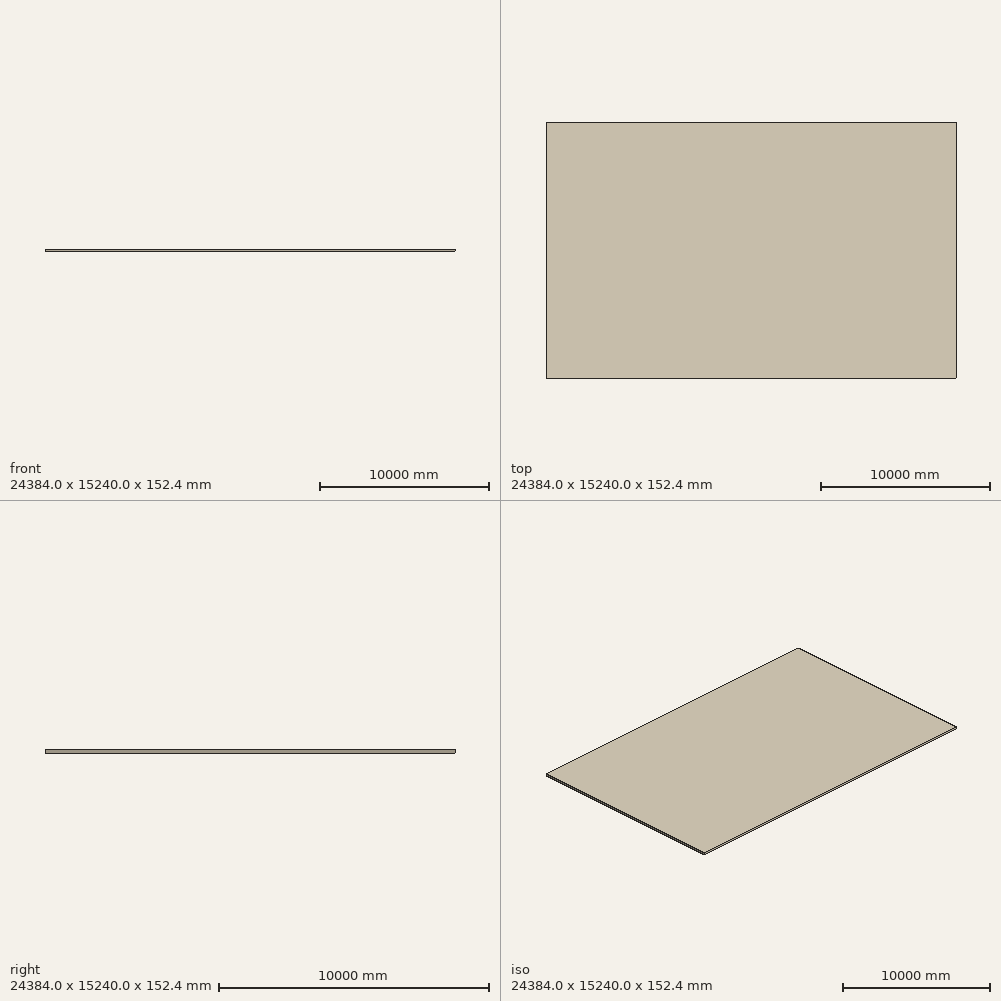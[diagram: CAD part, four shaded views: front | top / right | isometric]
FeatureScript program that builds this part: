
annotation { "Feature Type Name" : "Feature", "Feature Type Description" : "" }
export const myFeature = defineFeature(function(context is Context, id is Id, definition is map)
    precondition{}
    {
        {
            var Q0;
            Q0=qCreatedBy(makeId("Top.planeOp"),FACE);
            var sketch = newSketch(context, id + "F0", { "sketchPlane" : qUnion([Q0])});
            skLineSegment(sketch, "E0.bottom", {"start": v(-12192, 7620) * mm, "end": v(12192, 7620) * mm});
            skLineSegment(sketch, "E0.top", {"start": v(-12192, -7620) * mm, "end": v(12192, -7620) * mm});
            skLineSegment(sketch, "E0.left", {"start": v(-12192, 7620) * mm, "end": v(-12192, -7620) * mm});
            skLineSegment(sketch, "E0.right", {"start": v(12192, 7620) * mm, "end": v(12192, -7620) * mm});
            skSolve(sketch);
        }
        {
            var Q0;
            Q0=makeQuery(id+"F0.imprint","IMPRINT",FACE,{"disambiguationData":[TD([[makeQuery(id+"F0.imprint","IMPRINT",EDGE,{"derivedFrom":sQuery(id+"F0.wireOp",EDGE,"E0.bottom")}),-1.0]])]});
            extrude(context, id + "F1", {"entities" : qUnion([Q0]), "depth" : 152.4 * mm});
        }
        {
            var Q0;
            Q0=makeQuery(id+"F1.opExtrude","CAP_FACE",FACE,{"disambiguationData":[OSD([sQuery(id+"F0.wireOp",EDGE,"E0.bottom"),sQuery(id+"F0.wireOp",EDGE,"E0.top"),sQuery(id+"F0.wireOp",EDGE,"E0.left"),sQuery(id+"F0.wireOp",EDGE,"E0.right")])],"isStart":false});
            var sketch = newSketch(context, id + "F2", { "sketchPlane" : qUnion([Q0])});
            skLineSegment(sketch, "E1.bottom", {"start": v(-9753.6, 7467.6) * mm, "end": v(8534.4, 7467.6) * mm});
            skLineSegment(sketch, "E1.top", {"start": v(-9753.6, -5334) * mm, "end": v(8534.4, -5334) * mm});
            skLineSegment(sketch, "E1.left", {"start": v(-9753.6, 7467.6) * mm, "end": v(-9753.6, -5334) * mm});
            skLineSegment(sketch, "E1.right", {"start": v(8534.4, 7467.6) * mm, "end": v(8534.4, -5334) * mm});
            skSolve(sketch);
        }
        {
            var Q0;
            Q0 = qSketchRegion(id + "F2", true);
            var Q1;
            Q1 = qConstructionFilter(qBodyType(qCreatedBy(id + "F2" ,EDGE), BodyType.WIRE), ConstructionObject.NO);
            extrude(context, id + "F3", {"entities" : qUnion([Q0]), "bodyType" : ToolBodyType.SURFACE, "operationType" : NewBodyOperationType.ADD, "surfaceEntities" : qUnion([Q1]), "depth" : 5486.4 * mm});
        }
        {
            var Q0;
            Q0=makeQuery(id+"F3.opExtrude","SWEPT_FACE",FACE,{"disambiguationData":[OSD([sQuery(id+"F2.wireOp",EDGE,"E1.right")])]});
            var sketch = newSketch(context, id + "F4", { "sketchPlane" : qUnion([Q0])});
            skPoint(sketch, "E2.orphan", {"position": v(-7655.53, 5638.8) * mm});
            skPoint(sketch, "E3.start.orphan", {"position": v(-7655.53, 0) * mm});
            skLineSegment(sketch, "E4", {"start": v(1066.8, 10017.95) * mm, "end": v(-5334, 5638.8) * mm});
            skLineSegment(sketch, "E5", {"start": v(1066.8, 10017.95) * mm, "end": v(7467.6, 5638.8) * mm});
            skLineSegment(sketch, "E6", {"start": v(7467.6, 5638.8) * mm, "end": v(7622.71, 5532.68) * mm});
            skLineSegment(sketch, "E7", {"start": v(-5334, 5638.8) * mm, "end": v(-7655.53, 4909.86) * mm});
            skPoint(sketch, "E8.start.orphan", {"position": v(7622.71, 152.4) * mm});
            skSolve(sketch);
        }
        {
            var Q0;
            Q0 = qSketchRegion(id + "F4", true);
            var Q1;
            Q1 = qConstructionFilter(qBodyType(qCreatedBy(id + "F4" ,EDGE), BodyType.WIRE), ConstructionObject.NO);
            extrude(context, id + "F5", {"entities" : qUnion([Q0]), "bodyType" : ToolBodyType.SURFACE, "surfaceEntities" : qUnion([Q1]), "oppositeDirection" : true, "depth" : 20751.8 * mm});
        }
        {
            var Q0;
            Q0 = qSketchRegion(id + "F4", true);
            var Q1;
            Q1 = qConstructionFilter(qBodyType(qCreatedBy(id + "F4" ,EDGE), BodyType.WIRE), ConstructionObject.NO);
            extrude(context, id + "F6", {"entities" : qUnion([Q0]), "bodyType" : ToolBodyType.SURFACE, "operationType" : NewBodyOperationType.INTERSECT, "surfaceEntities" : qUnion([Q1]), "depth" : 3733.8 * mm});
        }
    });
